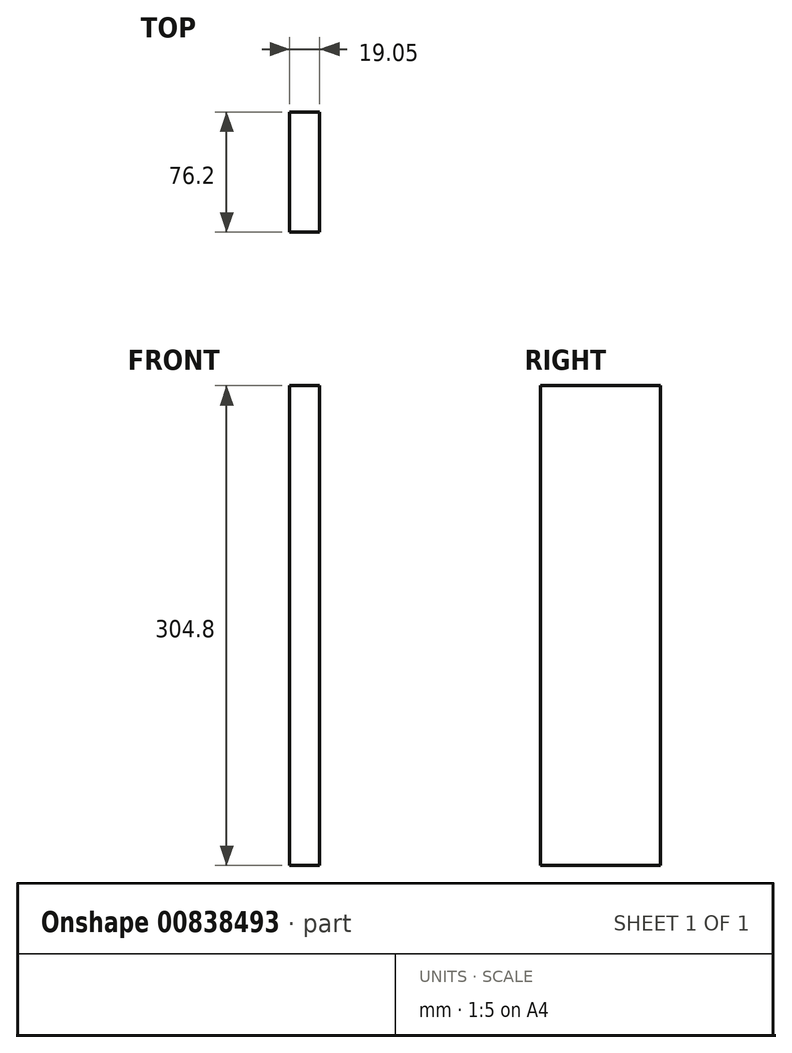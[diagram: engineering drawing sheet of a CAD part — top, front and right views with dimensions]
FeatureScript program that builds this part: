
annotation { "Feature Type Name" : "Feature", "Feature Type Description" : "" }
export const myFeature = defineFeature(function(context is Context, id is Id, definition is map)
    precondition{}
    {
        {
            var Q0;
            Q0=qCreatedBy(makeId("Right.planeOp"),FACE);
            var sketch = newSketch(context, id + "F0", { "sketchPlane" : qUnion([Q0])});
            skLineSegment(sketch, "E0.bottom", {"start": v(38.1, 152.4) * mm, "end": v(-38.1, 152.4) * mm});
            skLineSegment(sketch, "E0.top", {"start": v(38.1, -152.4) * mm, "end": v(-38.1, -152.4) * mm});
            skLineSegment(sketch, "E0.left", {"start": v(38.1, 152.4) * mm, "end": v(38.1, -152.4) * mm});
            skLineSegment(sketch, "E0.right", {"start": v(-38.1, 152.4) * mm, "end": v(-38.1, -152.4) * mm});
            skPoint(sketch, "E0.middle", {"position": v(0, 0) * mm});
            skSolve(sketch);
        }
        {
            var Q0;
            Q0 = qSketchRegion(id + "F0", true);
            extrude(context, id + "F1", {"entities" : qUnion([Q0]), "depth" : 19.05 * mm, "offsetDistance" : 25.4 * mm});
        }
    });
